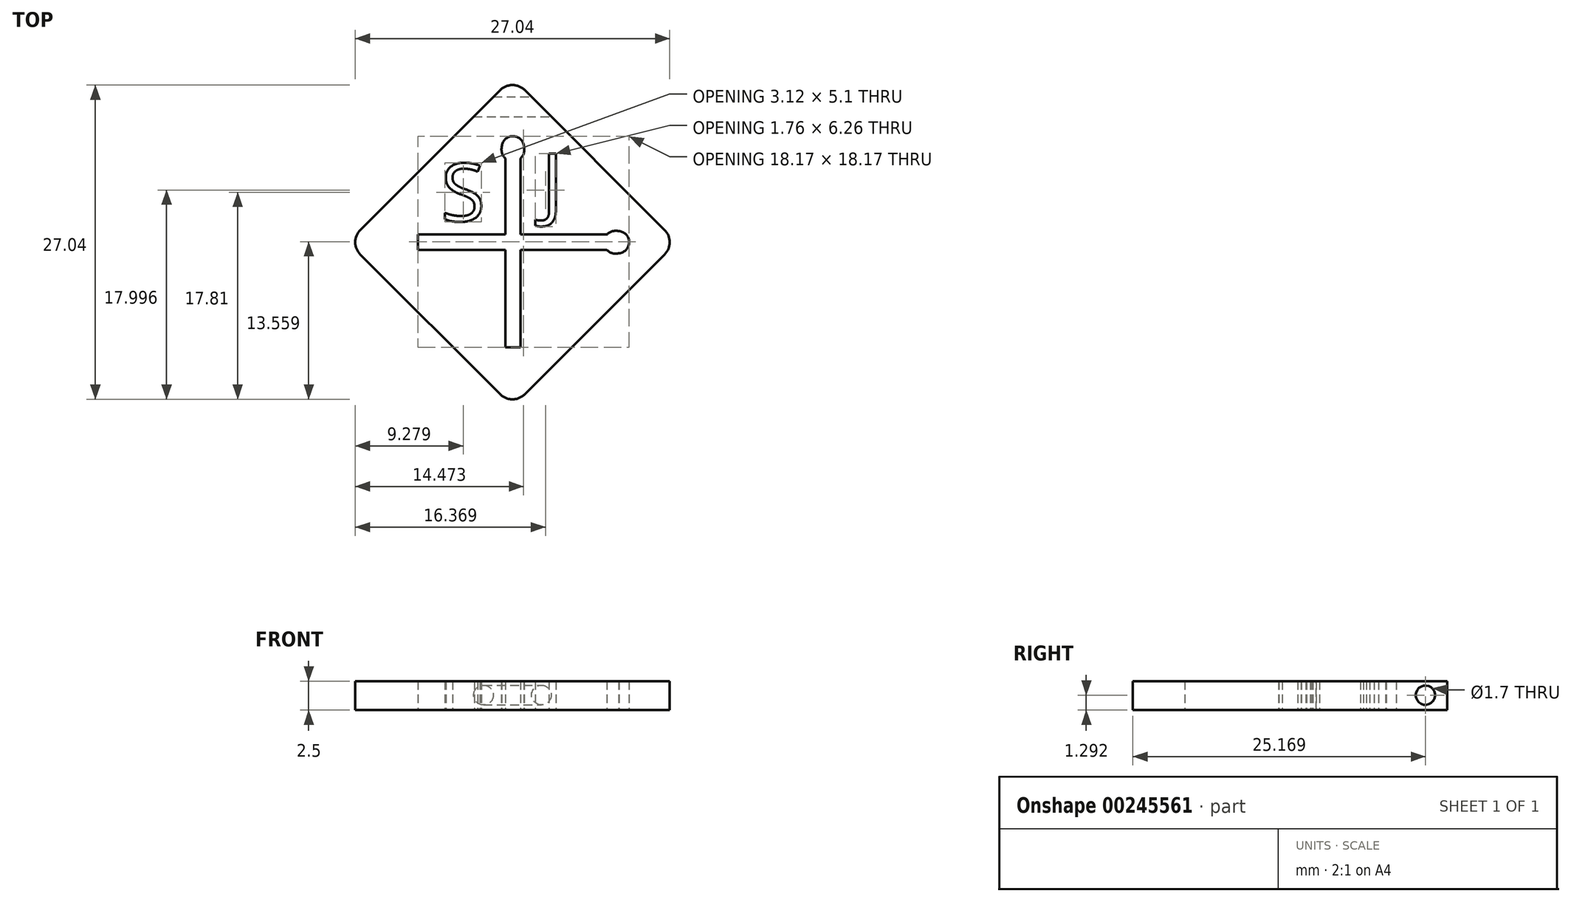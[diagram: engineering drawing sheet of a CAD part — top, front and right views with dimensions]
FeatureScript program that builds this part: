
annotation { "Feature Type Name" : "Feature", "Feature Type Description" : "" }
export const myFeature = defineFeature(function(context is Context, id is Id, definition is map)
    precondition{}
    {
        {
            var Q0;
            Q0=qCreatedBy(makeId("Top.planeOp"),FACE);
            var sketch = newSketch(context, id + "F0", { "sketchPlane" : qUnion([Q0])});
            skLineSegment(sketch, "E0", {"start": v(1.06, -1.06) * mm, "end": v(13.08, -13.08) * mm});
            skLineSegment(sketch, "E1", {"start": v(13.08, -15.2) * mm, "end": v(1.06, -27.22) * mm});
            skLineSegment(sketch, "E2", {"start": v(-1.06, -27.22) * mm, "end": v(-13.08, -15.2) * mm});
            skLineSegment(sketch, "E3", {"start": v(-13.08, -13.08) * mm, "end": v(-1.06, -1.06) * mm});
            skPoint(sketch, "E4.visualSharp", {"position": v(0, 0) * mm});
            skArc(sketch, "E4.filletArc", {"start": v(1.06, -1.06) * mm, "mid": v(0, -0.62) * mm, "end": v(-1.06, -1.06) * mm});
            skPoint(sketch, "E5.visualSharp", {"position": v(-14.14, -14.14) * mm});
            skArc(sketch, "E5.filletArc", {"start": v(-13.08, -13.08) * mm, "mid": v(-13.52, -14.14) * mm, "end": v(-13.08, -15.2) * mm});
            skPoint(sketch, "E6.visualSharp", {"position": v(14.14, -14.14) * mm});
            skArc(sketch, "E6.filletArc", {"start": v(13.08, -15.2) * mm, "mid": v(13.52, -14.14) * mm, "end": v(13.08, -13.08) * mm});
            skPoint(sketch, "E7.visualSharp", {"position": v(0, -28.28) * mm});
            skArc(sketch, "E7.filletArc", {"start": v(-1.06, -27.22) * mm, "mid": v(0, -27.66) * mm, "end": v(1.06, -27.22) * mm});
            skLineSegment(sketch, "E8", {"start": v(0, 0) * mm, "end": v(0, -31.86) * mm, "construction": true});
            skLineSegment(sketch, "E9", {"start": v(-14.14, -14.14) * mm, "end": v(14.14, -14.14) * mm, "construction": true});
            skLineSegment(sketch, "E10", {"start": v(-8.13, -13.48) * mm, "end": v(-8.13, -14.8) * mm});
            skLineSegment(sketch, "E11", {"start": v(-8.13, -14.8) * mm, "end": v(8.13, -14.8) * mm});
            skLineSegment(sketch, "E12", {"start": v(8.13, -13.48) * mm, "end": v(-8.13, -13.48) * mm});
            skLineSegment(sketch, "E13", {"start": v(-8.13, -13.48) * mm, "end": v(0, -13.48) * mm, "construction": true});
            skLineSegment(sketch, "E14", {"start": v(0, -13.48) * mm, "end": v(8.13, -13.48) * mm, "construction": true});
            skArc(sketch, "E15", {"start": v(9.18, -15.1) * mm, "mid": v(10.04, -14.12) * mm, "end": v(9.13, -13.2) * mm});
            skArc(sketch, "E16", {"start": v(9.13, -13.2) * mm, "mid": v(8.6, -13.2) * mm, "end": v(8.13, -13.48) * mm});
            skArc(sketch, "E17", {"start": v(8.13, -14.8) * mm, "mid": v(8.61, -15.1) * mm, "end": v(9.18, -15.1) * mm});
            skLineSegment(sketch, "E18", {"start": v(-0.62, -23.19) * mm, "end": v(0.7, -23.19) * mm});
            skLineSegment(sketch, "E19", {"start": v(0.7, -23.19) * mm, "end": v(0.7, -6.92) * mm});
            skLineSegment(sketch, "E20", {"start": v(-0.62, -6.92) * mm, "end": v(-0.62, -23.19) * mm});
            skLineSegment(sketch, "E21", {"start": v(-0.62, -23.19) * mm, "end": v(-0.62, -15.05) * mm, "construction": true});
            skLineSegment(sketch, "E22", {"start": v(-0.62, -15.05) * mm, "end": v(-0.62, -6.92) * mm, "construction": true});
            skArc(sketch, "E23", {"start": v(0.99, -5.88) * mm, "mid": v(0.02, -5.01) * mm, "end": v(-0.91, -5.92) * mm});
            skArc(sketch, "E24", {"start": v(-0.91, -5.92) * mm, "mid": v(-0.9, -6.46) * mm, "end": v(-0.62, -6.92) * mm});
            skArc(sketch, "E25", {"start": v(0.7, -6.92) * mm, "mid": v(1, -6.44) * mm, "end": v(0.99, -5.88) * mm});
            skText(sketch, "E26", { "text": "S\n", "fontName": "OpenSans-Regular.ttf"});
            skText(sketch, "E27", { "text": "J", "fontName": "OpenSans-Regular.ttf"});
            const initialGuessF0  = {"E26": [-0.00616, -0.01233, 1, 0, 0.005], "E27": [0.00251, -0.01149, 1, 0, 0.005]};
            skSetInitialGuess(sketch, initialGuessF0);
            skSolve(sketch);
        }
        {
            var Q0;
            Q0=makeQuery(id+"F0.imprint","IMPRINT",FACE,{"disambiguationData":[TD([[makeQuery(id+"F0.imprint","IMPRINT",EDGE,{"derivedFrom":sQuery(id+"F0.wireOp",EDGE,"E0")}),-1.0]])]});
            extrude(context, id + "F1", {"entities" : qUnion([Q0]), "depth" : 2.5 * mm});
        }
        {
            var Q0;
            Q0=qCreatedBy(makeId("Right.planeOp"),FACE);
            var sketch = newSketch(context, id + "F2", { "sketchPlane" : qUnion([Q0])});
            skCircle(sketch, "E28", {"center": v(-2.5, 1.3) * mm, "radius": 0.85 * mm});
            skSolve(sketch);
        }
        {
            var Q0;
            Q0=qSketchRegion(id+"F2",true);
            extrude(context, id + "F3", {"entities" : qUnion([Q0]), "operationType" : NewBodyOperationType.REMOVE, "endBound" : BoundingType.SYMMETRIC, "oppositeDirection" : true, "depth" : 25 * mm});
        }
    });
